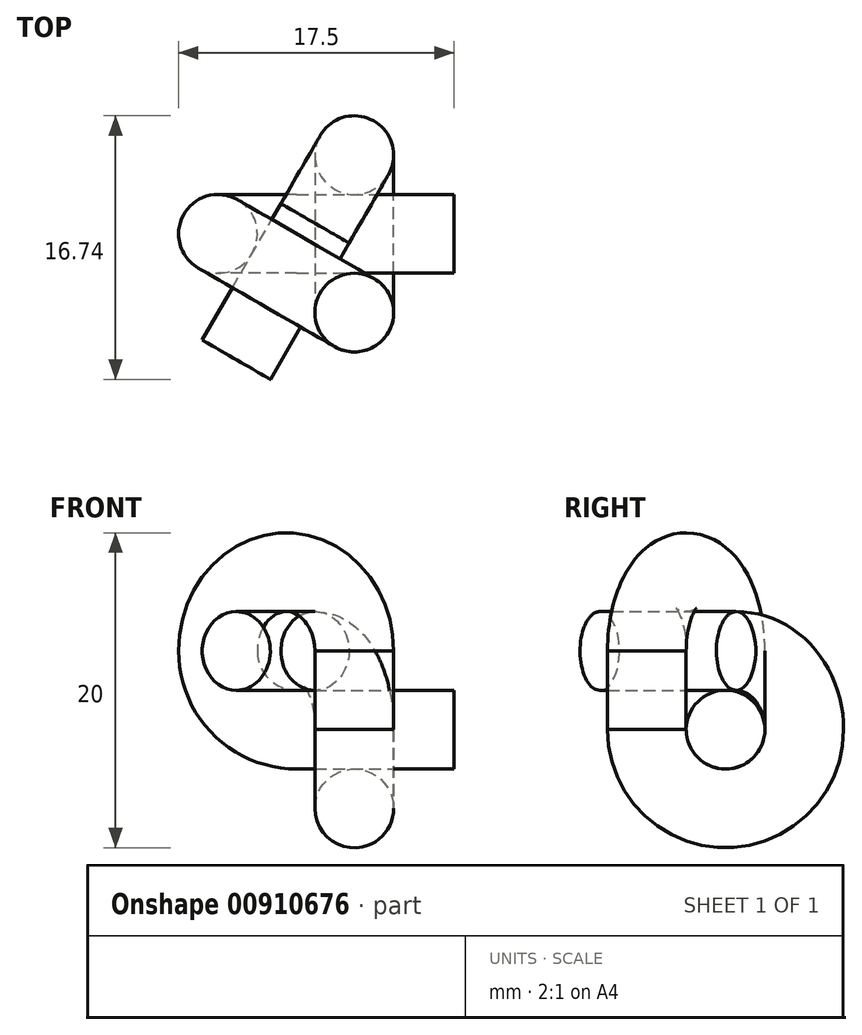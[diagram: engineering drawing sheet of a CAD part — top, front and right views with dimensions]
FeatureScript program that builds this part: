
annotation { "Feature Type Name" : "Feature", "Feature Type Description" : "" }
export const myFeature = defineFeature(function(context is Context, id is Id, definition is map)
    precondition{}
    {
        {
            var Q0;
            Q0=qCreatedBy(makeId("Right.planeOp"),FACE);
            var sketch = newSketch(context, id + "F0", { "sketchPlane" : qUnion([Q0])});
            skCircle(sketch, "E0", {"center": v(0, 0) * mm, "radius": 2.5 * mm});
            skSolve(sketch);
        }
        {
            var Q0;
            Q0 = qSketchRegion(id + "F0", true);
            extrude(context, id + "F1", {"entities" : qUnion([Q0]), "oppositeDirection" : true, "depth" : 5 * mm, "offsetDistance" : 25 * mm, "hasSecondDirection" : true, "secondDirectionOppositeDirection" : false, "secondDirectionDepth" : 5 * mm});
        }
        {
            var Q0;
            Q0=qCreatedBy(makeId("Front.planeOp"),FACE);
            var sketch = newSketch(context, id + "F2", { "sketchPlane" : qUnion([Q0])});
            skArc(sketch, "E1", {"start": v(-10, 5) * mm, "mid": v(-8.54, 1.46) * mm, "end": v(-5, 0) * mm});
            skSolve(sketch);
        }
        {
            var Q0;
            Q0=makeQuery(id+"F1.opExtrude","CAP_FACE",FACE,{"disambiguationData":[OSD([sQuery(id+"F0.wireOp",EDGE,"E0")])],"isStart":false});
            var Q1;
            Q1=sQuery(id+"F2.wireOp",EDGE,"E1");
            sweep(context, id + "F3", {"operationType" : NewBodyOperationType.ADD, "profiles" : qUnion([Q0]), "path" : qUnion([Q1])});
        }
        {
            var Q0;
            Q0=makeQuery(id+"F3.opSweep","CAP_FACE",FACE,{"disambiguationData":[OSD([sQuery(id+"F0.wireOp",EDGE,"E0"),sQuery(id+"F2.wireOp",VERTEX,"E1.start")])],"isStart":false});
            var sketch = newSketch(context, id + "F4", { "sketchPlane" : qUnion([Q0])});
            skCircle(sketch, "E2", {"center": v(-5.67, -2.5) * mm, "radius": 2.5 * mm});
            skCircle(sketch, "E3", {"center": v(-1.34, -5) * mm, "radius": 2.5 * mm});
            skLineSegment(sketch, "E4", {"start": v(0, 0) * mm, "end": v(0, -2.5) * mm});
            skLineSegment(sketch, "E5", {"start": v(0, -2.5) * mm, "end": v(-13.45, -2.5) * mm, "construction": true});
            skLineSegment(sketch, "E6", {"start": v(-1.34, -5) * mm, "end": v(-10, 0) * mm, "construction": true});
            skSolve(sketch);
        }
        {
            var Q0;
            Q0=sQuery(id+"F4.wireOp",EDGE,"E6");
            cPlane(context, id + "F5", {"entities" : qUnion([Q0]), "cplaneType" : CPlaneType.LINE_ANGLE, "offset" : 25 * mm, "angle" : 180 * degree, "oppositeDirection" : true, "width" : 150 * mm, "height" : 150 * mm});
        }
        {
            var Q0;
            Q0=qCreatedBy(id+"F5.planeOp",FACE);
            var sketch = newSketch(context, id + "F6", { "sketchPlane" : qUnion([Q0])});
            skArc(sketch, "E7", {"start": v(8.66, 5) * mm, "mid": v(3.66, 10) * mm, "end": v(-1.34, 5) * mm});
            skSolve(sketch);
        }
        {
            var Q0;
            Q0=makeQuery(id+"F4.imprint","IMPRINT",FACE,{"disambiguationData":[TD([[makeQuery(id+"F4.imprint","IMPRINT",EDGE,{"derivedFrom":makeQuery(id+"F3.opSweep","CAP_EDGE",EDGE,{"disambiguationData":[OSD([sQuery(id+"F0.wireOp",EDGE,"E0"),sQuery(id+"F2.wireOp",VERTEX,"E1.start")])],"isStart":false})}),1.0]])]});
            var Q1;
            Q1=sQuery(id+"F6.wireOp",EDGE,"E7");
            sweep(context, id + "F7", {"operationType" : NewBodyOperationType.ADD, "profiles" : qUnion([Q0]), "path" : qUnion([Q1])});
        }
        {
            var Q0;
            Q0=makeQuery(id+"F4.imprint","IMPRINT",FACE,{"disambiguationData":[TD([[makeQuery(id+"F4.imprint","IMPRINT",EDGE,{"derivedFrom":sQuery(id+"F4.wireOp",EDGE,"E3")}),1.0]])]});
            var Q1;
            Q1=makeQuery(id+"F1.opExtrude","SWEPT_FACE",FACE,{"disambiguationData":[OSD([sQuery(id+"F0.wireOp",EDGE,"E0")])]});
            extrude(context, id + "F8", {"entities" : qUnion([Q0]), "oppositeDirection" : true, "depth" : 5 * mm, "endBoundEntityFace" : qUnion([Q1]), "offsetDistance" : 25 * mm});
        }
        {
            var Q0;
            Q0=makeQuery(id+"F8.opExtrude","CAP_FACE",FACE,{"disambiguationData":[OSD([sQuery(id+"F4.wireOp",EDGE,"E3")])],"isStart":false});
            var sketch = newSketch(context, id + "F9", { "sketchPlane" : qUnion([Q0])});
            skLineSegment(sketch, "E8", {"start": v(-1.34, 5) * mm, "end": v(-1.34, -4.4) * mm, "construction": true});
            skSolve(sketch);
        }
        {
            var Q0;
            Q0=sQuery(id+"F9.wireOp",EDGE,"E8");
            cPlane(context, id + "F10", {"entities" : qUnion([Q0]), "cplaneType" : CPlaneType.LINE_ANGLE, "offset" : 25 * mm, "angle" : 90 * degree, "width" : 150 * mm, "height" : 150 * mm});
        }
        {
            var Q0;
            Q0=qCreatedBy(id+"F10.planeOp",FACE);
            var sketch = newSketch(context, id + "F11", { "sketchPlane" : qUnion([Q0])});
            skArc(sketch, "E9", {"start": v(-5, 0) * mm, "mid": v(0, -5) * mm, "end": v(5, 0) * mm});
            skLineSegment(sketch, "E10", {"start": v(0, 0) * mm, "end": v(0, -5) * mm, "construction": true});
            skLineSegment(sketch, "E11", {"start": v(5, 0) * mm, "end": v(-5, 0) * mm, "construction": true});
            skSolve(sketch);
        }
        {
            var Q0;
            Q0=makeQuery(id+"F9.imprint","IMPRINT",FACE,{"disambiguationData":[TD([[makeQuery(id+"F9.imprint","IMPRINT",EDGE,{"derivedFrom":makeQuery(id+"F8.opExtrude","CAP_EDGE",EDGE,{"disambiguationData":[OSD([sQuery(id+"F4.wireOp",EDGE,"E3")])],"isStart":false})}),-1.0]])]});
            var Q1;
            Q1=sQuery(id+"F11.wireOp",EDGE,"E9");
            sweep(context, id + "F12", {"profiles" : qUnion([Q0]), "path" : qUnion([Q1])});
        }
        {
            var Q0;
            Q0=makeQuery(id+"F12.opSweep","CAP_FACE",FACE,{"disambiguationData":[OSD([sQuery(id+"F4.wireOp",EDGE,"E3"),sQuery(id+"F11.wireOp",VERTEX,"E9.end")])],"isStart":false});
            var sketch = newSketch(context, id + "F13", { "sketchPlane" : qUnion([Q0])});
            skLineSegment(sketch, "E12", {"start": v(-1.34, 5) * mm, "end": v(-7.18, -5.12) * mm, "construction": true});
            skSolve(sketch);
        }
        {
            var Q0;
            Q0=sQuery(id+"F13.wireOp",EDGE,"E12");
            cPlane(context, id + "F14", {"entities" : qUnion([Q0]), "cplaneType" : CPlaneType.LINE_ANGLE, "offset" : 25 * mm, "angle" : 90 * degree, "width" : 150 * mm, "height" : 150 * mm});
        }
        {
            var Q0;
            Q0=qCreatedBy(id+"F14.planeOp",FACE);
            var sketch = newSketch(context, id + "F15", { "sketchPlane" : qUnion([Q0])});
            skArc(sketch, "E13", {"start": v(3.66, 0) * mm, "mid": v(2.2, 3.54) * mm, "end": v(-1.34, 5) * mm});
            skLineSegment(sketch, "E14", {"start": v(-1.34, 0) * mm, "end": v(-1.34, 5) * mm, "construction": true});
            skLineSegment(sketch, "E15", {"start": v(-1.34, 0) * mm, "end": v(3.66, 0) * mm, "construction": true});
            skSolve(sketch);
        }
        {
            var Q0;
            Q0=makeQuery(id+"F12.opSweep","CAP_FACE",FACE,{"disambiguationData":[OSD([sQuery(id+"F4.wireOp",EDGE,"E3"),sQuery(id+"F11.wireOp",VERTEX,"E9.end")])],"isStart":false});
            var Q1;
            Q1=sQuery(id+"F15.wireOp",EDGE,"E13");
            sweep(context, id + "F16", {"operationType" : NewBodyOperationType.ADD, "profiles" : qUnion([Q0]), "path" : qUnion([Q1])});
        }
        {
            var Q0;
            Q0=makeQuery(id+"F16.opSweep","CAP_FACE",FACE,{"disambiguationData":[OSD([sQuery(id+"F4.wireOp",EDGE,"E3"),sQuery(id+"F11.wireOp",VERTEX,"E9.end"),sQuery(id+"F15.wireOp",VERTEX,"E13.end")])],"isStart":false});
            extrude(context, id + "F17", {"entities" : qUnion([Q0]), "depth" : 10 * mm, "offsetDistance" : 25 * mm});
        }
    });
